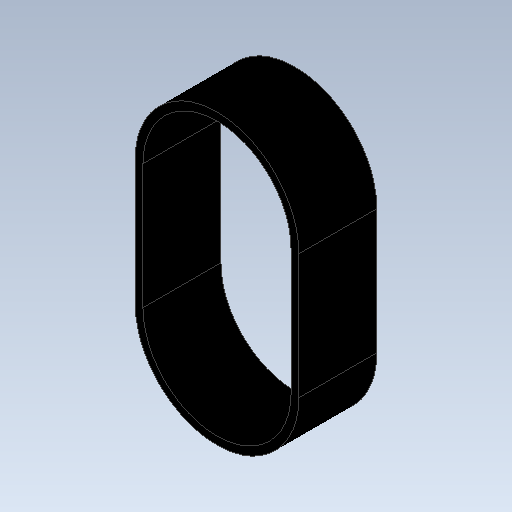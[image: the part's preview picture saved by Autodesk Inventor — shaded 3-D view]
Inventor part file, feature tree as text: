
AUTODESK INVENTOR PART (.ipt)
format: ipt  version: 2020 (Build 240168000, 168)  size: 109,056 bytes
history: native  units: mm
features: extrude x1, sketch x1
ambient origin geometry x8: Origin, YZ Plane, XZ Plane, XY Plane, X Axis, Y Axis, Z Axis, Center Point
bodies: Solid1 (feature_tree)
feature tree (2):
  extrude  "Extrusion1"  Depth=16.0mm
  sketch  "Sketch1"  dims[d3=9.5mm d4=16.0mm d5=1.0mm d6=10.0mm d7=0.0mm]
